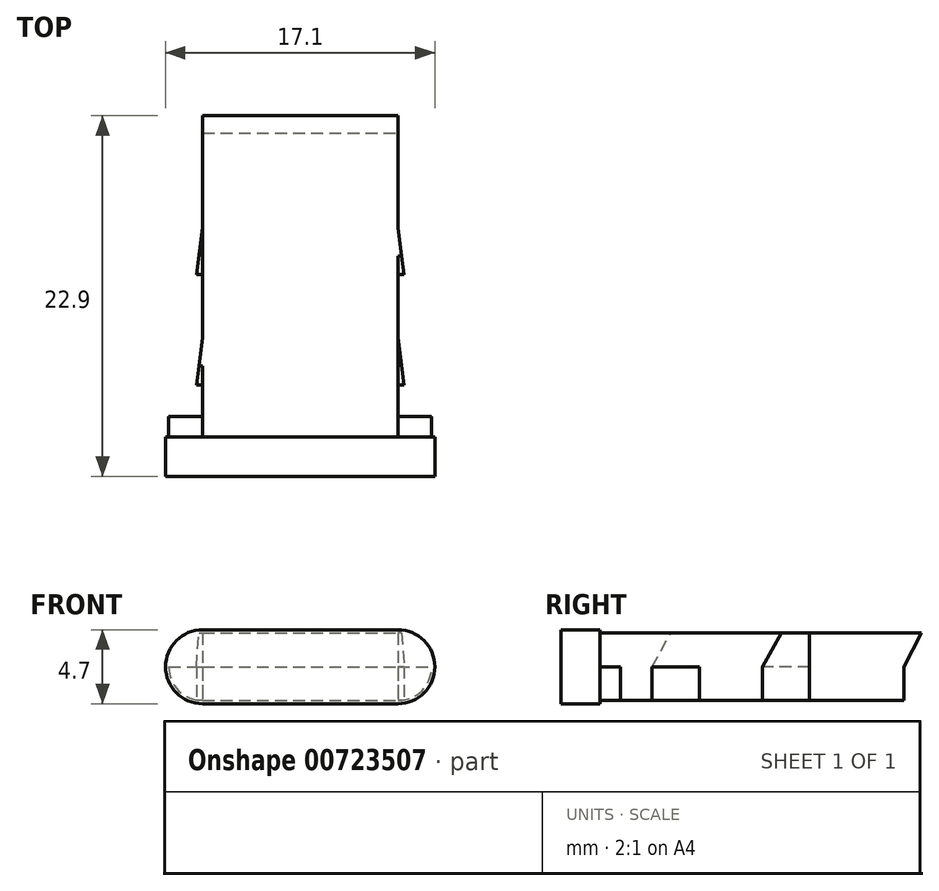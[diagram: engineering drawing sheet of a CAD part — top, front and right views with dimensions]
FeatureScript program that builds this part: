
annotation { "Feature Type Name" : "Feature", "Feature Type Description" : "" }
export const myFeature = defineFeature(function(context is Context, id is Id, definition is map)
    precondition{}
    {
        {
            var Q0;
            Q0=qCreatedBy(makeId("Top.planeOp"),FACE);
            var sketch = newSketch(context, id + "F0", { "sketchPlane" : qUnion([Q0])});
            skLineSegment(sketch, "E0.bottom", {"start": v(0, 0) * mm, "end": v(12.4, 0) * mm});
            skLineSegment(sketch, "E0.top", {"start": v(0, -18) * mm, "end": v(12.4, -18) * mm});
            skLineSegment(sketch, "E0.left", {"start": v(0, 0) * mm, "end": v(0, -18) * mm});
            skLineSegment(sketch, "E0.right", {"start": v(12.4, 0) * mm, "end": v(12.4, -18) * mm});
            skLineSegment(sketch, "E1", {"start": v(0, 0) * mm, "end": v(0, -16) * mm, "construction": true});
            skPoint(sketch, "E2", {"position": v(6.2, -18) * mm});
            skPoint(sketch, "E3", {"position": v(6.2, 0) * mm});
            skLineSegment(sketch, "E4", {"start": v(6.2, -18) * mm, "end": v(6.2, 0) * mm, "construction": true});
            skLineSegment(sketch, "E5", {"start": v(0, -16) * mm, "end": v(6.2, -16) * mm, "construction": true});
            skLineSegment(sketch, "E6", {"start": v(12.4, 0) * mm, "end": v(12.4, -9) * mm, "construction": true});
            skLineSegment(sketch, "E7", {"start": v(12.4, -9) * mm, "end": v(6.2, -9) * mm, "construction": true});
            skLineSegment(sketch, "E8", {"start": v(6.2, -16) * mm, "end": v(12.8, -16) * mm});
            skLineSegment(sketch, "E9.MirrorCS", {"start": v(6.2, -16) * mm, "end": v(-0.4, -16) * mm});
            skLineSegment(sketch, "E10", {"start": v(6.2, -9) * mm, "end": v(-0.4, -9) * mm});
            skLineSegment(sketch, "E11.MirrorCS", {"start": v(6.2, -9) * mm, "end": v(12.8, -9) * mm});
            skLineSegment(sketch, "E12", {"start": v(12.4, -16) * mm, "end": v(12.4, -13) * mm, "construction": true});
            skLineSegment(sketch, "E13", {"start": v(12.8, -16) * mm, "end": v(12.4, -13) * mm});
            skLineSegment(sketch, "E14", {"start": v(0, -9) * mm, "end": v(0, -6) * mm, "construction": true});
            skLineSegment(sketch, "E15", {"start": v(-0.4, -9) * mm, "end": v(0, -6) * mm});
            skLineSegment(sketch, "E16.MirrorCS", {"start": v(12.8, -9) * mm, "end": v(12.4, -6) * mm});
            skLineSegment(sketch, "E17.MirrorCS", {"start": v(-0.4, -16) * mm, "end": v(0, -13) * mm});
            skSolve(sketch);
        }
        {
            var Q0;
            Q0 = qSketchRegion(id + "F0", true);
            extrude(context, id + "F1", {"entities" : qUnion([Q0]), "depth" : 2.15 * mm, "offsetDistance" : 25 * mm});
        }
        {
            var Q0;
            Q0=makeQuery(id+"F1.opExtrude","CAP_FACE",FACE,{"disambiguationData":[OSD([sQuery(id+"F0.wireOp",EDGE,"E0.bottom"),sQuery(id+"F0.wireOp",EDGE,"E0.top"),sQuery(id+"F0.wireOp",EDGE,"E0.left"),sQuery(id+"F0.wireOp",EDGE,"E0.right"),sQuery(id+"F0.wireOp",EDGE,"E8"),sQuery(id+"F0.wireOp",EDGE,"E9.MirrorCS"),sQuery(id+"F0.wireOp",EDGE,"E10"),sQuery(id+"F0.wireOp",EDGE,"E11.MirrorCS"),sQuery(id+"F0.wireOp",EDGE,"E13"),sQuery(id+"F0.wireOp",EDGE,"E15"),sQuery(id+"F0.wireOp",EDGE,"E16.MirrorCS"),sQuery(id+"F0.wireOp",EDGE,"E17.MirrorCS")])],"isStart":false});
            var sketch = newSketch(context, id + "F2", { "sketchPlane" : qUnion([Q0])});
            skLineSegment(sketch, "E18.bottom", {"start": v(0, 0) * mm, "end": v(12.4, 0) * mm});
            skLineSegment(sketch, "E18.top", {"start": v(0, -19.3) * mm, "end": v(12.4, -19.3) * mm});
            skLineSegment(sketch, "E18.left", {"start": v(0, 0) * mm, "end": v(0, -19.3) * mm});
            skLineSegment(sketch, "E18.right", {"start": v(12.4, 0) * mm, "end": v(12.4, -19.3) * mm});
            skPoint(sketch, "E19", {"position": v(6.2, 0) * mm});
            skLineSegment(sketch, "E20", {"start": v(6.2, 0) * mm, "end": v(6.2, -19.3) * mm, "construction": true});
            skLineSegment(sketch, "E21", {"start": v(12.8, -9) * mm, "end": v(6.2, -9) * mm, "construction": true});
            skLineSegment(sketch, "E22", {"start": v(-0.4, -16) * mm, "end": v(6.2, -16) * mm, "construction": true});
            skSolve(sketch);
        }
        {
            var Q0;
            Q0 = qSketchRegion(id + "F2", true);
            extrude(context, id + "F3", {"entities" : qUnion([Q0]), "operationType" : NewBodyOperationType.ADD, "depth" : 2.15 * mm, "offsetDistance" : 25 * mm});
        }
        {
            var Q0;
            {var subQ0=sQuery(id+"F0.wireOp",EDGE,"E0.right");var subQ1=sQuery(id+"F0.wireOp",EDGE,"E0.top");var subQ2=sQuery(id+"F0.wireOp",EDGE,"E8");var subQ3=sQuery(id+"F0.wireOp",EDGE,"E11.MirrorCS");var subQ4=sQuery(id+"F0.wireOp",EDGE,"E13");var subQ5=sQuery(id+"F0.wireOp",EDGE,"E0.bottom");var subQ6=sQuery(id+"F0.wireOp",EDGE,"E16.MirrorCS");Q0=makeQuery(id+"F3.boolean.opBoolean","SPLIT",FACE,{"disambiguationData":[TD([makeQuery(id+"F1.opExtrude","SWEPT_FACE",FACE,{"disambiguationData":[OSD([subQ3])]})])],"derivedFrom":makeQuery(id+"F1.opExtrude","CAP_FACE",FACE,{"disambiguationData":[OSD([subQ5,subQ1,sQuery(id+"F0.wireOp",EDGE,"E0.left"),subQ0,subQ2,sQuery(id+"F0.wireOp",EDGE,"E9.MirrorCS"),sQuery(id+"F0.wireOp",EDGE,"E10"),subQ3,subQ4,sQuery(id+"F0.wireOp",EDGE,"E15"),subQ6,sQuery(id+"F0.wireOp",EDGE,"E17.MirrorCS")])],"isStart":false})});}
            extrude(context, id + "F4", {"entities" : qUnion([Q0]), "operationType" : NewBodyOperationType.ADD, "depth" : 2.15 * mm, "offsetDistance" : 25 * mm});
        }
        {
            var Q0;
            {var subQ5=sQuery(id+"F0.wireOp",EDGE,"E13");var subQ9=sQuery(id+"F0.wireOp",EDGE,"E0.right");var subQ11=sQuery(id+"F0.wireOp",EDGE,"E0.top");var subQ12=sQuery(id+"F0.wireOp",EDGE,"E0.bottom");var subQ13=sQuery(id+"F2.wireOp",EDGE,"E18.right");Q0=makeQuery(id+"F4.boolean.opBoolean","SPLIT",FACE,{"disambiguationData":[TD([makeQuery(id+"F1.opExtrude","SWEPT_FACE",FACE,{"disambiguationData":[OSD([subQ11])]})])],"derivedFrom":makeQuery(id+"F3.boolean.opBoolean","MERGE",FACE,{"derivedFrom":[makeQuery(id+"F1.opExtrude","SWEPT_FACE",FACE,{"disambiguationData":[OSD([subQ9]),TDD([makeQuery(id+"F0.imprint","IMPRINT",EDGE,{"disambiguationData":[TD([[makeQuery(id+"F0.imprint","INTERSECT",VERTEX,{"derivedFrom":[subQ12,subQ9]}),-1.0]])],"derivedFrom":subQ9})])]}),makeQuery(id+"F1.opExtrude","SWEPT_FACE",FACE,{"disambiguationData":[OSD([subQ9]),TDD([makeQuery(id+"F0.imprint","IMPRINT",EDGE,{"disambiguationData":[TD([[makeQuery(id+"F0.imprint","INTERSECT",VERTEX,{"derivedFrom":[subQ9,subQ5]}),1.0]])],"derivedFrom":subQ9})])]}),makeQuery(id+"F1.opExtrude","SWEPT_FACE",FACE,{"disambiguationData":[OSD([subQ9]),TDD([makeQuery(id+"F0.imprint","IMPRINT",EDGE,{"disambiguationData":[TD([[makeQuery(id+"F0.imprint","INTERSECT",VERTEX,{"derivedFrom":[subQ11,subQ9]}),1.0]])],"derivedFrom":subQ9})])]}),makeQuery(id+"F3.opExtrude","SWEPT_FACE",FACE,{"disambiguationData":[OSD([subQ13])]})]})});}
            var sketch = newSketch(context, id + "F5", { "sketchPlane" : qUnion([Q0])});
            skLineSegment(sketch, "E23", {"start": v(-9, 2.15) * mm, "end": v(-9, 4.3) * mm});
            skLineSegment(sketch, "E24", {"start": v(-9, 4.3) * mm, "end": v(-7.8, 4.3) * mm});
            skLineSegment(sketch, "E25", {"start": v(-7.8, 4.3) * mm, "end": v(-9, 2.15) * mm});
            skSolve(sketch);
        }
        {
            var Q0;
            Q0 = qSketchRegion(id + "F5", true);
            extrude(context, id + "F6", {"entities" : qUnion([Q0]), "operationType" : NewBodyOperationType.REMOVE, "depth" : 25 * mm, "offsetDistance" : 25 * mm});
        }
        {
            var Q0;
            {var subQ0=sQuery(id+"F0.wireOp",EDGE,"E9.MirrorCS");var subQ1=sQuery(id+"F0.wireOp",EDGE,"E0.left");var subQ2=sQuery(id+"F0.wireOp",EDGE,"E0.top");var subQ3=sQuery(id+"F0.wireOp",EDGE,"E17.MirrorCS");var subQ4=sQuery(id+"F0.wireOp",EDGE,"E10");var subQ5=sQuery(id+"F0.wireOp",EDGE,"E0.bottom");var subQ6=sQuery(id+"F0.wireOp",EDGE,"E15");Q0=makeQuery(id+"F3.boolean.opBoolean","SPLIT",FACE,{"disambiguationData":[TD([makeQuery(id+"F1.opExtrude","SWEPT_FACE",FACE,{"disambiguationData":[OSD([subQ0])]})])],"derivedFrom":makeQuery(id+"F1.opExtrude","CAP_FACE",FACE,{"disambiguationData":[OSD([subQ5,subQ2,subQ1,sQuery(id+"F0.wireOp",EDGE,"E0.right"),sQuery(id+"F0.wireOp",EDGE,"E8"),subQ0,subQ4,sQuery(id+"F0.wireOp",EDGE,"E11.MirrorCS"),sQuery(id+"F0.wireOp",EDGE,"E13"),subQ6,sQuery(id+"F0.wireOp",EDGE,"E16.MirrorCS"),subQ3])],"isStart":false})});}
            extrude(context, id + "F7", {"entities" : qUnion([Q0]), "operationType" : NewBodyOperationType.ADD, "depth" : 2.15 * mm, "offsetDistance" : 25 * mm});
        }
        {
            var Q0;
            {var subQ1=sQuery(id+"F2.wireOp",EDGE,"E18.left");var subQ4=sQuery(id+"F0.wireOp",EDGE,"E17.MirrorCS");var subQ13=sQuery(id+"F0.wireOp",EDGE,"E0.left");var subQ14=sQuery(id+"F0.wireOp",EDGE,"E0.top");var subQ15=sQuery(id+"F0.wireOp",EDGE,"E0.bottom");Q0=makeQuery(id+"F7.boolean.opBoolean","SPLIT",FACE,{"disambiguationData":[TD([makeQuery(id+"F1.opExtrude","SWEPT_FACE",FACE,{"disambiguationData":[OSD([subQ14])]})])],"derivedFrom":makeQuery(id+"F3.boolean.opBoolean","MERGE",FACE,{"derivedFrom":[makeQuery(id+"F1.opExtrude","SWEPT_FACE",FACE,{"disambiguationData":[OSD([subQ13]),TDD([makeQuery(id+"F0.imprint","IMPRINT",EDGE,{"disambiguationData":[TD([[makeQuery(id+"F0.imprint","INTERSECT",VERTEX,{"derivedFrom":[subQ15,subQ13]}),-1.0]])],"derivedFrom":subQ13})])]}),makeQuery(id+"F1.opExtrude","SWEPT_FACE",FACE,{"disambiguationData":[OSD([subQ13]),TDD([makeQuery(id+"F0.imprint","IMPRINT",EDGE,{"disambiguationData":[TD([[makeQuery(id+"F0.imprint","INTERSECT",VERTEX,{"derivedFrom":[subQ13,subQ4]}),1.0]])],"derivedFrom":subQ13})])]}),makeQuery(id+"F1.opExtrude","SWEPT_FACE",FACE,{"disambiguationData":[OSD([subQ13]),TDD([makeQuery(id+"F0.imprint","IMPRINT",EDGE,{"disambiguationData":[TD([[makeQuery(id+"F0.imprint","INTERSECT",VERTEX,{"derivedFrom":[subQ14,subQ13]}),1.0]])],"derivedFrom":subQ13})])]}),makeQuery(id+"F3.opExtrude","SWEPT_FACE",FACE,{"disambiguationData":[OSD([subQ1])]})]})});}
            var sketch = newSketch(context, id + "F8", { "sketchPlane" : qUnion([Q0])});
            skLineSegment(sketch, "E26", {"start": v(16, 2.15) * mm, "end": v(16, 4.3) * mm});
            skLineSegment(sketch, "E27", {"start": v(16, 4.3) * mm, "end": v(14.8, 4.3) * mm});
            skLineSegment(sketch, "E28", {"start": v(14.8, 4.3) * mm, "end": v(16, 2.15) * mm});
            skSolve(sketch);
        }
        {
            var Q0;
            Q0 = qSketchRegion(id + "F8", true);
            extrude(context, id + "F9", {"entities" : qUnion([Q0]), "operationType" : NewBodyOperationType.REMOVE, "depth" : 25 * mm, "offsetDistance" : 25 * mm});
        }
        {
            var Q0;
            {var subQ4=sQuery(id+"F0.wireOp",EDGE,"E13");var subQ9=sQuery(id+"F0.wireOp",EDGE,"E0.right");var subQ11=sQuery(id+"F0.wireOp",EDGE,"E0.top");var subQ12=sQuery(id+"F0.wireOp",EDGE,"E0.bottom");var subQ13=sQuery(id+"F2.wireOp",EDGE,"E18.right");Q0=makeQuery(id+"F4.boolean.opBoolean","SPLIT",FACE,{"disambiguationData":[TD([makeQuery(id+"F1.opExtrude","SWEPT_FACE",FACE,{"disambiguationData":[OSD([subQ12])]})])],"derivedFrom":makeQuery(id+"F3.boolean.opBoolean","MERGE",FACE,{"derivedFrom":[makeQuery(id+"F1.opExtrude","SWEPT_FACE",FACE,{"disambiguationData":[OSD([subQ9]),TDD([makeQuery(id+"F0.imprint","IMPRINT",EDGE,{"disambiguationData":[TD([[makeQuery(id+"F0.imprint","INTERSECT",VERTEX,{"derivedFrom":[subQ12,subQ9]}),-1.0]])],"derivedFrom":subQ9})])]}),makeQuery(id+"F1.opExtrude","SWEPT_FACE",FACE,{"disambiguationData":[OSD([subQ9]),TDD([makeQuery(id+"F0.imprint","IMPRINT",EDGE,{"disambiguationData":[TD([[makeQuery(id+"F0.imprint","INTERSECT",VERTEX,{"derivedFrom":[subQ9,subQ4]}),1.0]])],"derivedFrom":subQ9})])]}),makeQuery(id+"F1.opExtrude","SWEPT_FACE",FACE,{"disambiguationData":[OSD([subQ9]),TDD([makeQuery(id+"F0.imprint","IMPRINT",EDGE,{"disambiguationData":[TD([[makeQuery(id+"F0.imprint","INTERSECT",VERTEX,{"derivedFrom":[subQ11,subQ9]}),1.0]])],"derivedFrom":subQ9})])]}),makeQuery(id+"F3.opExtrude","SWEPT_FACE",FACE,{"disambiguationData":[OSD([subQ13])]})]})});}
            var sketch = newSketch(context, id + "F10", { "sketchPlane" : qUnion([Q0])});
            skLineSegment(sketch, "E29", {"start": v(0, 4.3) * mm, "end": v(0, 2.15) * mm});
            skLineSegment(sketch, "E30", {"start": v(0, 2.15) * mm, "end": v(1.1, 4.3) * mm});
            skLineSegment(sketch, "E31", {"start": v(1.1, 4.3) * mm, "end": v(0, 4.3) * mm});
            skSolve(sketch);
        }
        {
            var Q0;
            Q0 = qSketchRegion(id + "F10", true);
            var Q1;
            Q1=makeQuery(id+"F3.opExtrude","CAP_VERTEX",VERTEX,{"disambiguationData":[OSD([sQuery(id+"F2.wireOp",EDGE,"E18.bottom"),sQuery(id+"F2.wireOp",EDGE,"E18.left")])],"isStart":false});
            extrude(context, id + "F11", {"entities" : qUnion([Q0]), "operationType" : NewBodyOperationType.ADD, "endBound" : BoundingType.UP_TO_VERTEX, "oppositeDirection" : true, "depth" : 25 * mm, "endBoundEntityVertex" : qUnion([Q1]), "offsetDistance" : 25 * mm});
        }
        {
            var Q0;
            Q0=makeQuery(id+"F3.opExtrude","SWEPT_FACE",FACE,{"disambiguationData":[OSD([sQuery(id+"F2.wireOp",EDGE,"E18.top")])]});
            var sketch = newSketch(context, id + "F12", { "sketchPlane" : qUnion([Q0])});
            skCircle(sketch, "E32", {"center": v(0, 2.15) * mm, "radius": 2.15 * mm});
            skCircle(sketch, "E33", {"center": v(12.4, 2.15) * mm, "radius": 2.15 * mm});
            skLineSegment(sketch, "E34", {"start": v(0, 0) * mm, "end": v(12.4, 0) * mm});
            skLineSegment(sketch, "E35", {"start": v(0, 2.15) * mm, "end": v(-2.15, 2.15) * mm});
            skLineSegment(sketch, "E36", {"start": v(12.4, 2.15) * mm, "end": v(14.55, 2.15) * mm});
            skLineSegment(sketch, "E37", {"start": v(0, 2.15) * mm, "end": v(12.4, 2.15) * mm});
            skSolve(sketch);
        }
        {
            var Q0;
            Q0 = qSketchRegion(id + "F12", true);
            var Q1;
            {var subQ3=sQuery(id+"F2.wireOp",EDGE,"E18.top");var subQ5=makeQuery(id+"F3.opExtrude","CAP_EDGE",EDGE,{"disambiguationData":[OSD([subQ3])],"isStart":false});Q1=makeQuery(id+"F12.imprint","IMPRINT",FACE,{"disambiguationData":[TD([[makeQuery(id+"F12.imprint","IMPRINT",EDGE,{"derivedFrom":subQ5}),-1.0]])]});}
            var Q2;
            {var subQ0=sQuery(id+"F12.wireOp",EDGE,"E34");Q2=makeQuery(id+"F12.imprint","IMPRINT",FACE,{"disambiguationData":[TD([[makeQuery(id+"F12.imprint","IMPRINT",EDGE,{"derivedFrom":subQ0}),1.0]])]});}
            extrude(context, id + "F13", {"entities" : qUnion([Q0, Q1, Q2]), "operationType" : NewBodyOperationType.ADD, "depth" : 2.5 * mm, "offsetDistance" : 25 * mm});
        }
        {
            var Q0;
            {var subQ2=sQuery(id+"F12.wireOp",EDGE,"E35");Q0=makeQuery(id+"F12.imprint","IMPRINT",FACE,{"disambiguationData":[TD([[makeQuery(id+"F12.imprint","IMPRINT",EDGE,{"derivedFrom":subQ2}),1.0]])]});}
            var Q1;
            {var subQ0=sQuery(id+"F12.wireOp",EDGE,"E34");Q1=makeQuery(id+"F12.imprint","IMPRINT",FACE,{"disambiguationData":[TD([[makeQuery(id+"F12.imprint","IMPRINT",EDGE,{"derivedFrom":subQ0}),1.0]])]});}
            var Q2;
            {var subQ4=sQuery(id+"F12.wireOp",EDGE,"E36");Q2=makeQuery(id+"F12.imprint","IMPRINT",FACE,{"disambiguationData":[TD([[makeQuery(id+"F12.imprint","IMPRINT",EDGE,{"derivedFrom":subQ4}),-1.0]])]});}
            extrude(context, id + "F14", {"entities" : qUnion([Q0, Q1, Q2]), "operationType" : NewBodyOperationType.ADD, "oppositeDirection" : true, "depth" : 1.3 * mm, "offsetDistance" : 25 * mm});
        }
        {
            var Q0;
            Q0=makeQuery(id+"F13.opExtrude","CAP_FACE",FACE,{"disambiguationData":[OSD([sQuery(id+"F2.wireOp",EDGE,"E18.top"),sQuery(id+"F12.wireOp",EDGE,"E32"),sQuery(id+"F12.wireOp",EDGE,"E33"),sQuery(id+"F12.wireOp",EDGE,"E34")])],"isStart":false});
            var sketch = newSketch(context, id + "F15", { "sketchPlane" : qUnion([Q0])});
            skLineSegment(sketch, "E38.0", {"start": v(12.4, 4.5) * mm, "end": v(0, 4.5) * mm});
            skArc(sketch, "E38.1", {"start": v(12.4, -0.2) * mm, "mid": v(14.75, 2.15) * mm, "end": v(12.4, 4.5) * mm});
            skLineSegment(sketch, "E38.2", {"start": v(0, -0.2) * mm, "end": v(12.4, -0.2) * mm});
            skArc(sketch, "E38.3", {"start": v(0, 4.5) * mm, "mid": v(-2.35, 2.15) * mm, "end": v(0, -0.2) * mm});
            skSolve(sketch);
        }
        {
            var Q0;
            Q0 = qSketchRegion(id + "F15", true);
            extrude(context, id + "F16", {"entities" : qUnion([Q0]), "operationType" : NewBodyOperationType.ADD, "oppositeDirection" : true, "depth" : 2.5 * mm, "offsetDistance" : 25 * mm});
        }
    });
